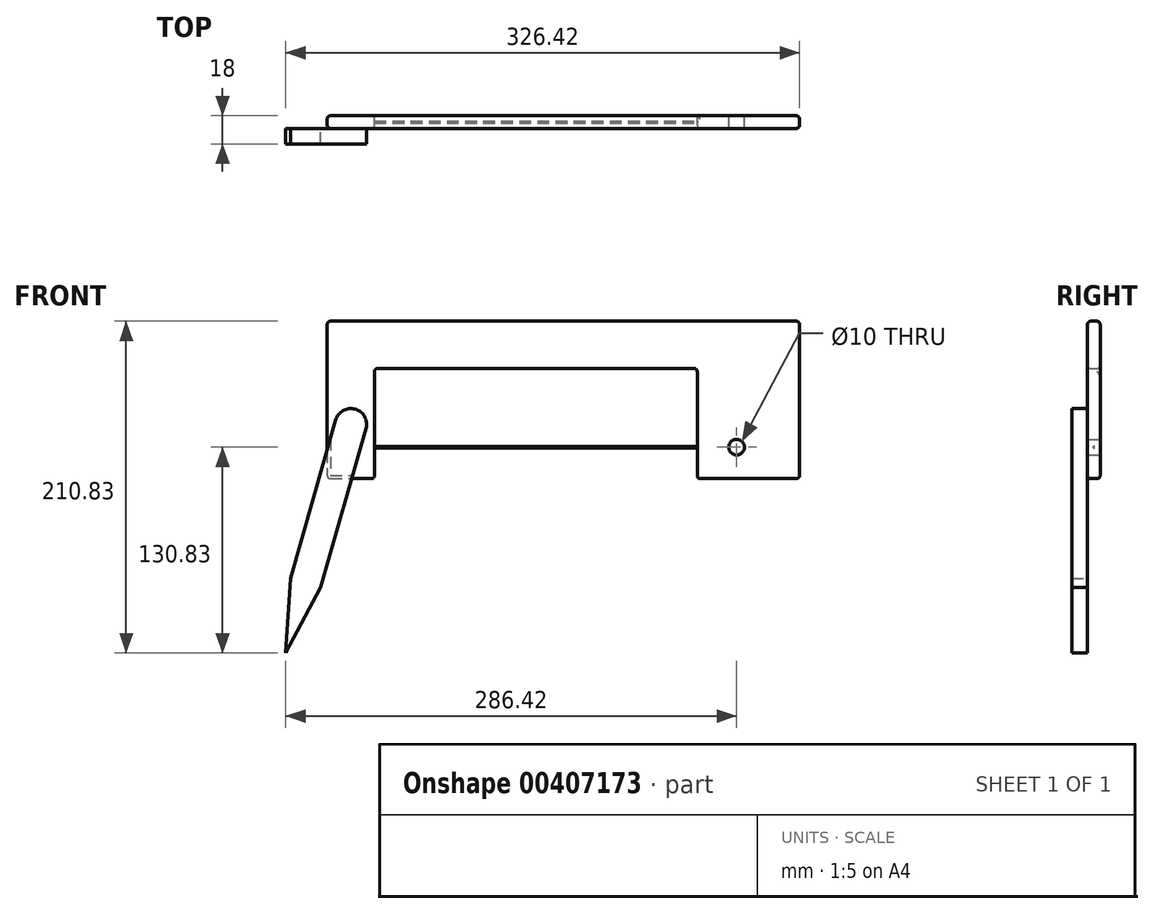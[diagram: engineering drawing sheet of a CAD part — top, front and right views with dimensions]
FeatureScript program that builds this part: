
annotation { "Feature Type Name" : "Feature", "Feature Type Description" : "" }
export const myFeature = defineFeature(function(context is Context, id is Id, definition is map)
    precondition{}
    {
        {
            var Q0;
            Q0=qCreatedBy(makeId("Front.planeOp"),FACE);
            var sketch = newSketch(context, id + "F0", { "sketchPlane" : qUnion([Q0])});
            skCircle(sketch, "E0", {"center": v(0, 0) * mm, "radius": 5 * mm});
            skLineSegment(sketch, "E1", {"start": v(-25, -20) * mm, "end": v(40, -20) * mm});
            skLineSegment(sketch, "E2", {"start": v(40, -20) * mm, "end": v(40, 80) * mm});
            skLineSegment(sketch, "E3", {"start": v(40, 80) * mm, "end": v(-260, 80) * mm});
            skLineSegment(sketch, "E4", {"start": v(-260, 80) * mm, "end": v(-260, -20) * mm});
            skLineSegment(sketch, "E5", {"start": v(-260, -20) * mm, "end": v(-230, -20) * mm});
            skLineSegment(sketch, "E6", {"start": v(-230, -20) * mm, "end": v(-230, 50) * mm});
            skLineSegment(sketch, "E7", {"start": v(-230, 50) * mm, "end": v(-25, 50) * mm});
            skLineSegment(sketch, "E8", {"start": v(-25, 50) * mm, "end": v(-25, -20) * mm});
            skSolve(sketch);
        }
        {
            var Q0;
            Q0=makeQuery(id+"F0.imprint","IMPRINT",FACE,{"disambiguationData":[TD([[makeQuery(id+"F0.imprint","IMPRINT",EDGE,{"derivedFrom":sQuery(id+"F0.wireOp",EDGE,"E0")}),-1.0]])]});
            extrude(context, id + "F1", {"entities" : qUnion([Q0]), "depth" : 8 * mm, "offsetDistance" : 25 * mm});
        }
        {
            var Q0;
            Q0=makeQuery(id+"F1.opExtrude","CAP_EDGE",EDGE,{"disambiguationData":[OSD([sQuery(id+"F0.wireOp",EDGE,"E4")])],"isStart":false});
            var Q1;
            Q1=makeQuery(id+"F1.opExtrude","CAP_EDGE",EDGE,{"disambiguationData":[OSD([sQuery(id+"F0.wireOp",EDGE,"E5")])],"isStart":false});
            var Q2;
            Q2=makeQuery(id+"F1.opExtrude","CAP_EDGE",EDGE,{"disambiguationData":[OSD([sQuery(id+"F0.wireOp",EDGE,"E6")])],"isStart":false});
            var Q3;
            Q3=makeQuery(id+"F1.opExtrude","CAP_EDGE",EDGE,{"disambiguationData":[OSD([sQuery(id+"F0.wireOp",EDGE,"E7")])],"isStart":false});
            var Q4;
            Q4=makeQuery(id+"F1.opExtrude","CAP_EDGE",EDGE,{"disambiguationData":[OSD([sQuery(id+"F0.wireOp",EDGE,"E8")])],"isStart":false});
            var Q5;
            Q5=makeQuery(id+"F1.opExtrude","CAP_EDGE",EDGE,{"disambiguationData":[OSD([sQuery(id+"F0.wireOp",EDGE,"E1")])],"isStart":false});
            var Q6;
            Q6=makeQuery(id+"F1.opExtrude","CAP_EDGE",EDGE,{"disambiguationData":[OSD([sQuery(id+"F0.wireOp",EDGE,"E2")])],"isStart":false});
            var Q7;
            Q7=makeQuery(id+"F1.opExtrude","CAP_EDGE",EDGE,{"disambiguationData":[OSD([sQuery(id+"F0.wireOp",EDGE,"E3")])],"isStart":false});
            var Q8;
            Q8=makeQuery(id+"F1.opExtrude","SWEPT_EDGE",EDGE,{"disambiguationData":[OSD([sQuery(id+"F0.wireOp",EDGE,"E3"),sQuery(id+"F0.wireOp",EDGE,"E4")])]});
            var Q9;
            Q9=makeQuery(id+"F1.opExtrude","SWEPT_EDGE",EDGE,{"disambiguationData":[OSD([sQuery(id+"F0.wireOp",EDGE,"E4"),sQuery(id+"F0.wireOp",EDGE,"E5")])]});
            var Q10;
            Q10=makeQuery(id+"F1.opExtrude","SWEPT_EDGE",EDGE,{"disambiguationData":[OSD([sQuery(id+"F0.wireOp",EDGE,"E2"),sQuery(id+"F0.wireOp",EDGE,"E3")])]});
            var Q11;
            Q11=makeQuery(id+"F1.opExtrude","SWEPT_EDGE",EDGE,{"disambiguationData":[OSD([sQuery(id+"F0.wireOp",EDGE,"E1"),sQuery(id+"F0.wireOp",EDGE,"E2")])]});
            var Q12;
            Q12=makeQuery(id+"F1.opExtrude","SWEPT_EDGE",EDGE,{"disambiguationData":[OSD([sQuery(id+"F0.wireOp",EDGE,"E1"),sQuery(id+"F0.wireOp",EDGE,"E8")])]});
            var Q13;
            Q13=makeQuery(id+"F1.opExtrude","SWEPT_EDGE",EDGE,{"disambiguationData":[OSD([sQuery(id+"F0.wireOp",EDGE,"E7"),sQuery(id+"F0.wireOp",EDGE,"E8")])]});
            var Q14;
            Q14=makeQuery(id+"F1.opExtrude","SWEPT_EDGE",EDGE,{"disambiguationData":[OSD([sQuery(id+"F0.wireOp",EDGE,"E6"),sQuery(id+"F0.wireOp",EDGE,"E7")])]});
            var Q15;
            Q15=makeQuery(id+"F1.opExtrude","SWEPT_EDGE",EDGE,{"disambiguationData":[OSD([sQuery(id+"F0.wireOp",EDGE,"E5"),sQuery(id+"F0.wireOp",EDGE,"E6")])]});
            var Q16;
            Q16=makeQuery(id+"F1.opExtrude","CAP_EDGE",EDGE,{"disambiguationData":[OSD([sQuery(id+"F0.wireOp",EDGE,"E5")])],"isStart":true});
            var Q17;
            Q17=makeQuery(id+"F1.opExtrude","CAP_EDGE",EDGE,{"disambiguationData":[OSD([sQuery(id+"F0.wireOp",EDGE,"E6")])],"isStart":true});
            var Q18;
            Q18=makeQuery(id+"F1.opExtrude","CAP_EDGE",EDGE,{"disambiguationData":[OSD([sQuery(id+"F0.wireOp",EDGE,"E7")])],"isStart":true});
            var Q19;
            Q19=makeQuery(id+"F1.opExtrude","CAP_EDGE",EDGE,{"disambiguationData":[OSD([sQuery(id+"F0.wireOp",EDGE,"E1")])],"isStart":true});
            var Q20;
            Q20=makeQuery(id+"F1.opExtrude","CAP_EDGE",EDGE,{"disambiguationData":[OSD([sQuery(id+"F0.wireOp",EDGE,"E2")])],"isStart":true});
            var Q21;
            Q21=makeQuery(id+"F1.opExtrude","CAP_EDGE",EDGE,{"disambiguationData":[OSD([sQuery(id+"F0.wireOp",EDGE,"E3")])],"isStart":true});
            var Q22;
            Q22=makeQuery(id+"F1.opExtrude","CAP_EDGE",EDGE,{"disambiguationData":[OSD([sQuery(id+"F0.wireOp",EDGE,"E4")])],"isStart":true});
            fillet(context, id + "F2", {"entities" : qUnion([Q0, Q1, Q2, Q3, Q4, Q5, Q6, Q7, Q8, Q9, Q10, Q11, Q12, Q13, Q14, Q15, Q16, Q17, Q18, Q19, Q20, Q21, Q22]), "radius" : 2 * mm, "tangentPropagation" : true, "allowEdgeOverflow" : false});
        }
        {
            var Q0;
            Q0=makeQuery(id+"F1.opExtrude","SWEPT_FACE",FACE,{"disambiguationData":[OSD([sQuery(id+"F0.wireOp",EDGE,"E8")])]});
            var sketch = newSketch(context, id + "F3", { "sketchPlane" : qUnion([Q0])});
            skCircle(sketch, "E9", {"center": v(4, 0) * mm, "radius": 0.5 * mm});
            skPoint(sketch, "E9.centerSnap0", {"position": v(4, -18) * mm});
            skSolve(sketch);
        }
        {
            var Q0;
            Q0=makeQuery(id+"F3.imprint","IMPRINT",FACE,{"disambiguationData":[TD([[makeQuery(id+"F3.imprint","IMPRINT",EDGE,{"derivedFrom":sQuery(id+"F3.wireOp",EDGE,"E9")}),1.0]])]});
            var Q1;
            Q1=makeQuery(id+"F1.opExtrude","SWEPT_FACE",FACE,{"disambiguationData":[OSD([sQuery(id+"F0.wireOp",EDGE,"E6")])]});
            extrude(context, id + "F4", {"entities" : qUnion([Q0]), "operationType" : NewBodyOperationType.ADD, "endBound" : BoundingType.UP_TO_SURFACE, "depth" : 25 * mm, "endBoundEntityFace" : qUnion([Q1]), "offsetDistance" : 25 * mm});
        }
        {
            var Q0;
            Q0=makeQuery(id+"F1.opExtrude","CAP_FACE",FACE,{"disambiguationData":[OSD([sQuery(id+"F0.wireOp",EDGE,"E0"),sQuery(id+"F0.wireOp",EDGE,"E1"),sQuery(id+"F0.wireOp",EDGE,"E2"),sQuery(id+"F0.wireOp",EDGE,"E3"),sQuery(id+"F0.wireOp",EDGE,"E4"),sQuery(id+"F0.wireOp",EDGE,"E5"),sQuery(id+"F0.wireOp",EDGE,"E6"),sQuery(id+"F0.wireOp",EDGE,"E7"),sQuery(id+"F0.wireOp",EDGE,"E8")])],"isStart":false});
            var sketch = newSketch(context, id + "F5", { "sketchPlane" : qUnion([Q0])});
            skLineSegment(sketch, "E10", {"start": v(-245, -19.95) * mm, "end": v(-245, 14.49) * mm, "construction": true});
            skPoint(sketch, "E10.startSnap0", {"position": v(-245, -18) * mm});
            skPoint(sketch, "E10.endSnap0", {"position": v(-245, -18) * mm});
            skLineSegment(sketch, "E11", {"start": v(-245, 14.49) * mm, "end": v(-283.68, -121.21) * mm, "construction": true});
            skArc(sketch, "E12.0.startCap", {"start": v(-254.62, 17.23) * mm, "mid": v(-242.26, 24.1) * mm, "end": v(-235.38, 11.75) * mm});
            skLineSegment(sketch, "E12.0.left", {"start": v(-235.38, 11.75) * mm, "end": v(-264.1, -89) * mm});
            skLineSegment(sketch, "E12.0.right", {"start": v(-254.62, 17.23) * mm, "end": v(-283.33, -83.5) * mm});
            skPoint(sketch, "E13.0", {"position": v(0, 0) * mm});
            skLineSegment(sketch, "E14", {"start": v(-25, -0.5) * mm, "end": v(-230, -0.5) * mm});
            skLineSegment(sketch, "E15", {"start": v(-283.68, -121.21) * mm, "end": v(-286.42, -130.83) * mm});
            skLineSegment(sketch, "E16", {"start": v(0, 0) * mm, "end": v(-286.42, -130.83) * mm, "construction": true});
            skLineSegment(sketch, "E17", {"start": v(-283.33, -83.5) * mm, "end": v(-286.42, -130.83) * mm});
            skLineSegment(sketch, "E18", {"start": v(-264.1, -89) * mm, "end": v(-286.42, -130.83) * mm});
            skSolve(sketch);
        }
        {
            var Q0;
            Q0 = qSketchRegion(id + "F5", true);
            extrude(context, id + "F6", {"entities" : qUnion([Q0]), "operationType" : NewBodyOperationType.ADD, "depth" : 10 * mm, "offsetDistance" : 25 * mm});
        }
    });
